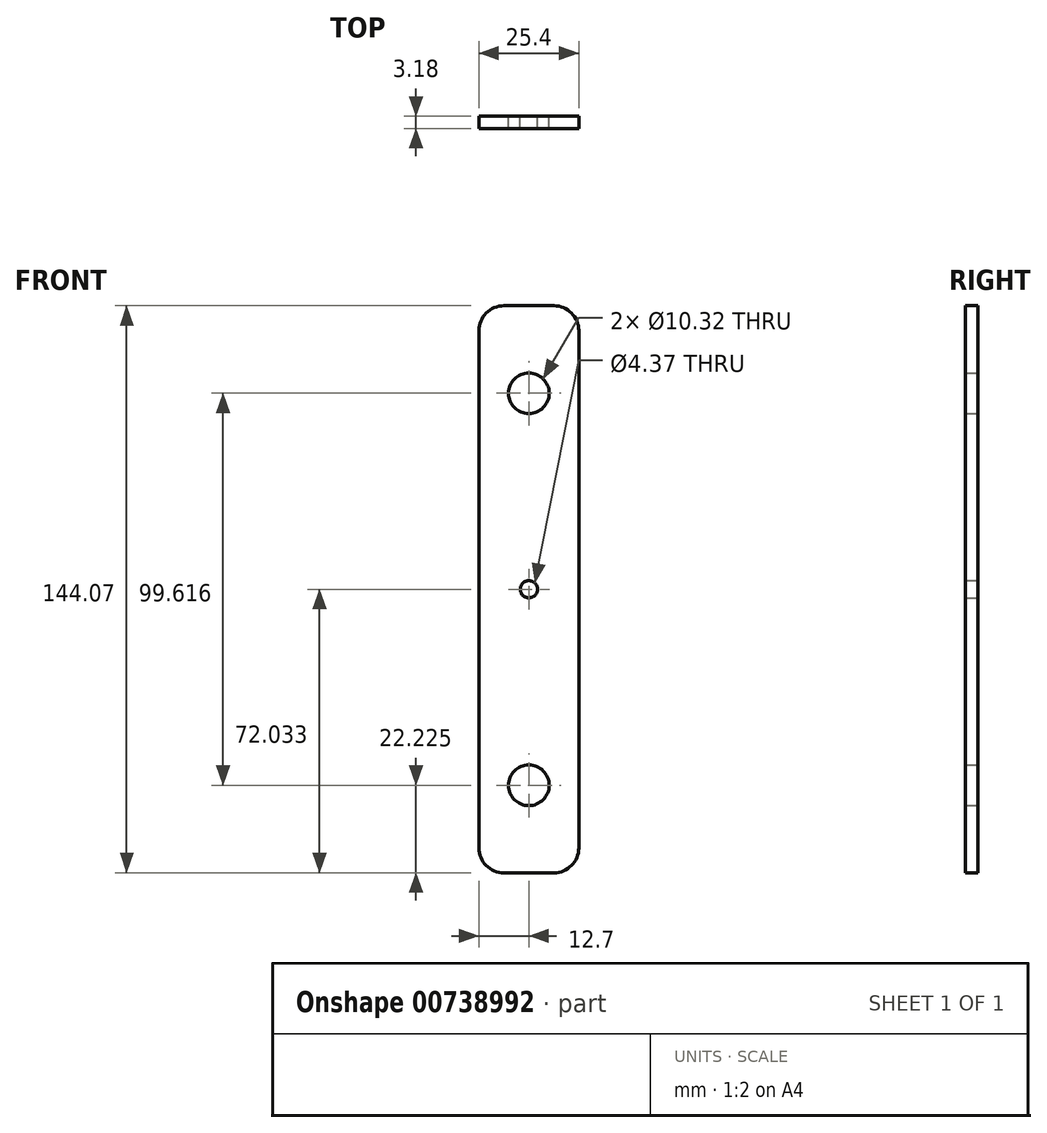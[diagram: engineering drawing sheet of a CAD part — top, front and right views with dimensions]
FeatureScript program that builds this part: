
annotation { "Feature Type Name" : "Feature", "Feature Type Description" : "" }
export const myFeature = defineFeature(function(context is Context, id is Id, definition is map)
    precondition{}
    {
        {
            var Q0;
            Q0=qCreatedBy(makeId("Front.planeOp"),FACE);
            var sketch = newSketch(context, id + "F0", { "sketchPlane" : qUnion([Q0])});
            skLineSegment(sketch, "E0.bottom", {"start": v(6.35, 0) * mm, "end": v(19.05, 0) * mm});
            skLineSegment(sketch, "E0.top", {"start": v(6.35, 144.07) * mm, "end": v(19.05, 144.07) * mm});
            skLineSegment(sketch, "E0.left", {"start": v(0, 6.35) * mm, "end": v(0, 137.72) * mm});
            skLineSegment(sketch, "E0.right", {"start": v(25.4, 6.35) * mm, "end": v(25.4, 137.72) * mm});
            skCircle(sketch, "E1", {"center": v(12.7, 22.23) * mm, "radius": 5.16 * mm});
            skPoint(sketch, "E1.centerSnap0", {"position": v(12.7, 0) * mm});
            skCircle(sketch, "E2", {"center": v(12.7, 72.03) * mm, "radius": 2.18 * mm});
            skCircle(sketch, "E3", {"center": v(12.7, 121.84) * mm, "radius": 5.16 * mm});
            skPoint(sketch, "E4.visualSharp", {"position": v(25.4, 0) * mm});
            skArc(sketch, "E4.filletArc", {"start": v(19.05, 0) * mm, "mid": v(23.54, 1.86) * mm, "end": v(25.4, 6.35) * mm});
            skPoint(sketch, "E5.visualSharp", {"position": v(0, 0) * mm});
            skArc(sketch, "E5.filletArc", {"start": v(0, 6.35) * mm, "mid": v(1.86, 1.86) * mm, "end": v(6.35, 0) * mm});
            skPoint(sketch, "E6.visualSharp", {"position": v(0, 144.07) * mm});
            skArc(sketch, "E6.filletArc", {"start": v(6.35, 144.07) * mm, "mid": v(1.86, 142.2) * mm, "end": v(0, 137.72) * mm});
            skPoint(sketch, "E7.visualSharp", {"position": v(25.4, 144.07) * mm});
            skArc(sketch, "E7.filletArc", {"start": v(25.4, 137.72) * mm, "mid": v(23.54, 142.2) * mm, "end": v(19.05, 144.07) * mm});
            skSolve(sketch);
        }
        {
            var Q0;
            Q0 = qSketchRegion(id + "F0", true);
            extrude(context, id + "F1", {"entities" : qUnion([Q0]), "depth" : 3.17 * mm, "offsetDistance" : 25.4 * mm});
        }
    });
